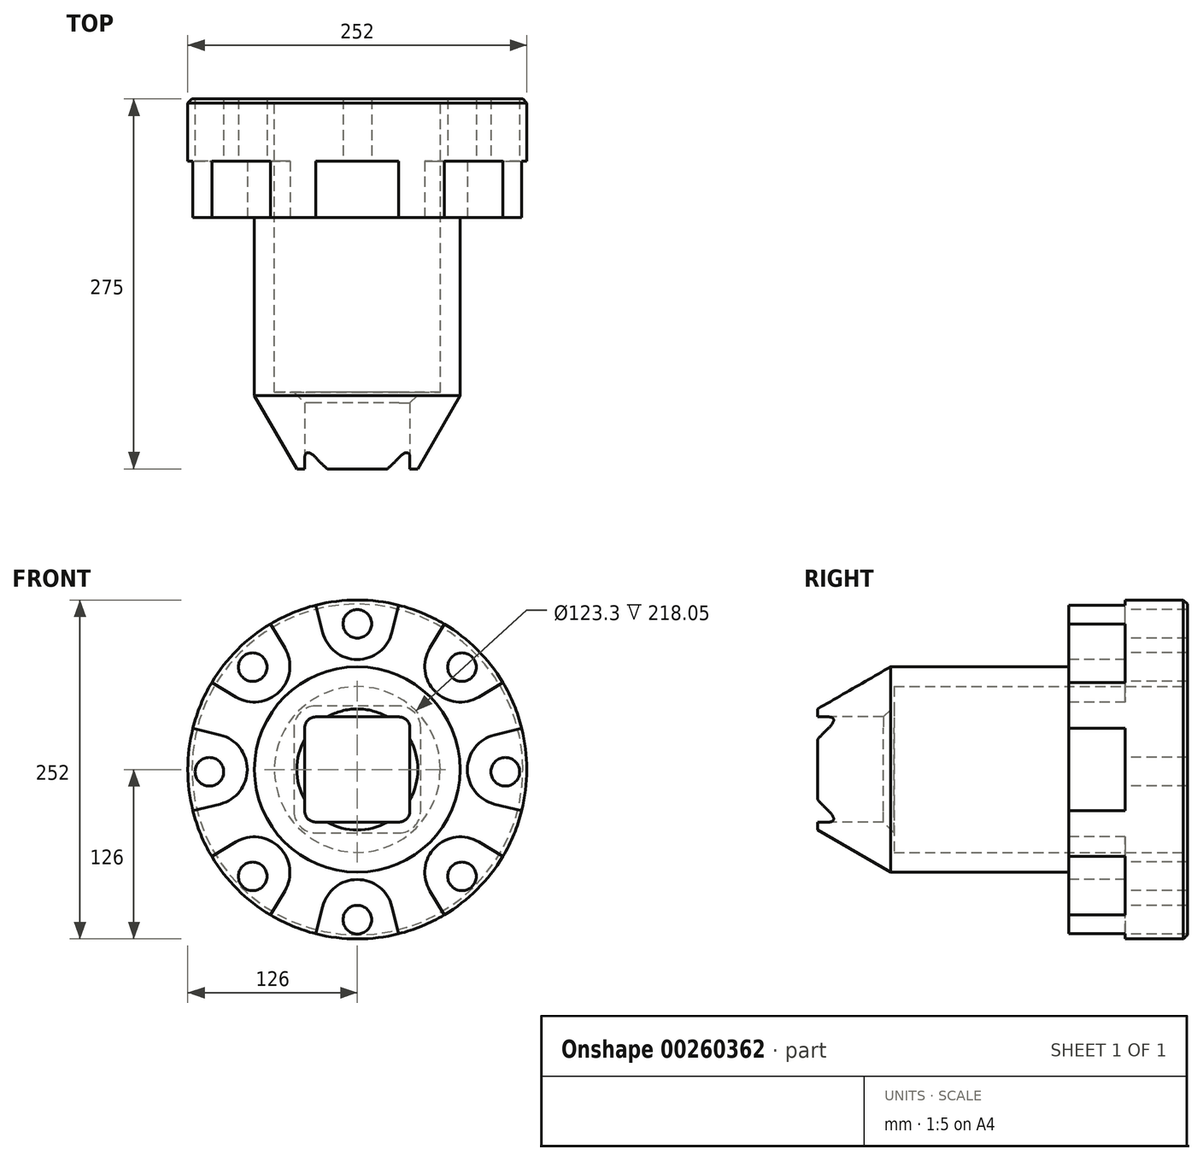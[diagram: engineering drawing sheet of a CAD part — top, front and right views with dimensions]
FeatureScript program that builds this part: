
annotation { "Feature Type Name" : "Feature", "Feature Type Description" : "" }
export const myFeature = defineFeature(function(context is Context, id is Id, definition is map)
    precondition{}
    {
        {
            var Q0;
            Q0=qCreatedBy(makeId("Front.planeOp"),FACE);
            var sketch = newSketch(context, id + "F0", { "sketchPlane" : qUnion([Q0])});
            skCircle(sketch, "E0", {"center": v(0, 0) * mm, "radius": 126 * mm});
            skSolve(sketch);
        }
        {
            var Q0;
            Q0 = qSketchRegion(id + "F0", true);
            extrude(context, id + "F1", {"entities" : qUnion([Q0]), "depth" : 275 * mm});
        }
        {
            var Q0;
            Q0=makeQuery(id+"F1.opExtrude","CAP_FACE",FACE,{"disambiguationData":[OSD([sQuery(id+"F0.wireOp",EDGE,"E0")])],"isStart":false});
            var sketch = newSketch(context, id + "F2", { "sketchPlane" : qUnion([Q0])});
            skCircle(sketch, "E1", {"center": v(0, 0) * mm, "radius": 76.45 * mm});
            skSolve(sketch);
        }
        {
            var Q0;
            Q0=makeQuery(id+"F2.imprint","IMPRINT",FACE,{"disambiguationData":[TD([[makeQuery(id+"F2.imprint","IMPRINT",EDGE,{"derivedFrom":sQuery(id+"F2.wireOp",EDGE,"E1")}),-1.0]])]});
            extrude(context, id + "F3", {"entities" : qUnion([Q0]), "operationType" : NewBodyOperationType.REMOVE, "oppositeDirection" : true, "depth" : (275 - 88.25) * mm});
        }
        {
            var Q0;
            Q0=makeQuery(id+"F3.boolean.opBoolean","COPY",FACE,{"derivedFrom":makeQuery(id+"F3.opExtrude","CAP_FACE",FACE,{"disambiguationData":[OSD([sQuery(id+"F0.wireOp",EDGE,"E0"),sQuery(id+"F2.wireOp",EDGE,"E1")])],"isStart":false})});
            var sketch = newSketch(context, id + "F4", { "sketchPlane" : qUnion([Q0])});
            skCircle(sketch, "E2", {"center": v(0, 108.32) * mm, "radius": 10.62 * mm});
            skCircle(sketch, "E3.1.0", {"center": v(-77.78, 76.1) * mm, "radius": 10.62 * mm});
            skCircle(sketch, "E3.2.0", {"center": v(-110, -1.68) * mm, "radius": 10.62 * mm});
            skCircle(sketch, "E3.3.0", {"center": v(-77.78, -79.46) * mm, "radius": 10.62 * mm});
            skCircle(sketch, "E3.4.0", {"center": v(0, -111.68) * mm, "radius": 10.62 * mm});
            skCircle(sketch, "E3.5.0", {"center": v(77.78, -79.46) * mm, "radius": 10.62 * mm});
            skCircle(sketch, "E3.6.0", {"center": v(110, -1.68) * mm, "radius": 10.62 * mm});
            skCircle(sketch, "E3.7.0", {"center": v(77.78, 76.1) * mm, "radius": 10.62 * mm});
            skPoint(sketch, "E3.center", {"position": v(0, -1.68) * mm});
            skSolve(sketch);
        }
        {
            var Q0;
            Q0 = qSketchRegion(id + "F4", true);
            extrude(context, id + "F5", {"entities" : qUnion([Q0]), "operationType" : NewBodyOperationType.REMOVE, "oppositeDirection" : true, "depth" : 25 * mm});
        }
        {
            var Q0;
            Q0 = qSketchRegion(id + "F4", true);
            extrude(context, id + "F6", {"entities" : qUnion([Q0]), "operationType" : NewBodyOperationType.REMOVE, "oppositeDirection" : true, "depth" : 169 * mm});
        }
        {
            var Q0;
            Q0=makeQuery(id+"F3.boolean.opBoolean","COPY",FACE,{"derivedFrom":makeQuery(id+"F3.opExtrude","CAP_FACE",FACE,{"disambiguationData":[OSD([sQuery(id+"F0.wireOp",EDGE,"E0"),sQuery(id+"F2.wireOp",EDGE,"E1")])],"isStart":false})});
            var sketch = newSketch(context, id + "F7", { "sketchPlane" : qUnion([Q0])});
            skPoint(sketch, "E4.center", {"position": v(0, 0) * mm});
            skArc(sketch, "E5", {"start": v(-25.71, 101.9) * mm, "mid": v(0, 81.82) * mm, "end": v(25.71, 101.9) * mm});
            skLineSegment(sketch, "E6", {"start": v(25.71, 101.9) * mm, "end": v(36.8, 146.37) * mm});
            skLineSegment(sketch, "E7", {"start": v(36.8, 146.37) * mm, "end": v(-36.8, 146.37) * mm});
            skLineSegment(sketch, "E8.MirrorCS", {"start": v(-25.71, 101.9) * mm, "end": v(-36.8, 146.37) * mm});
            skLineSegment(sketch, "E9.1.0", {"start": v(-77.48, 129.52) * mm, "end": v(-129.52, 77.48) * mm});
            skLineSegment(sketch, "E9.1.1", {"start": v(-53.88, 90.24) * mm, "end": v(-77.48, 129.52) * mm});
            skArc(sketch, "E9.1.2", {"start": v(-90.24, 53.88) * mm, "mid": v(-57.85, 57.85) * mm, "end": v(-53.88, 90.24) * mm});
            skLineSegment(sketch, "E9.1.3", {"start": v(-90.24, 53.88) * mm, "end": v(-129.52, 77.48) * mm});
            skLineSegment(sketch, "E9.2.0", {"start": v(-146.37, 36.8) * mm, "end": v(-146.37, -36.8) * mm});
            skLineSegment(sketch, "E9.2.1", {"start": v(-101.9, 25.71) * mm, "end": v(-146.37, 36.8) * mm});
            skArc(sketch, "E9.2.2", {"start": v(-101.9, -25.71) * mm, "mid": v(-81.82, 0) * mm, "end": v(-101.9, 25.71) * mm});
            skLineSegment(sketch, "E9.2.3", {"start": v(-101.9, -25.71) * mm, "end": v(-146.37, -36.8) * mm});
            skLineSegment(sketch, "E9.3.0", {"start": v(-129.52, -77.48) * mm, "end": v(-77.48, -129.52) * mm});
            skLineSegment(sketch, "E9.3.1", {"start": v(-90.24, -53.88) * mm, "end": v(-129.52, -77.48) * mm});
            skArc(sketch, "E9.3.2", {"start": v(-53.88, -90.24) * mm, "mid": v(-57.85, -57.85) * mm, "end": v(-90.24, -53.88) * mm});
            skLineSegment(sketch, "E9.3.3", {"start": v(-53.88, -90.24) * mm, "end": v(-77.48, -129.52) * mm});
            skLineSegment(sketch, "E9.4.0", {"start": v(-36.8, -146.37) * mm, "end": v(36.8, -146.37) * mm});
            skLineSegment(sketch, "E9.4.1", {"start": v(-25.71, -101.9) * mm, "end": v(-36.8, -146.37) * mm});
            skArc(sketch, "E9.4.2", {"start": v(25.71, -101.9) * mm, "mid": v(0, -81.82) * mm, "end": v(-25.71, -101.9) * mm});
            skLineSegment(sketch, "E9.4.3", {"start": v(25.71, -101.9) * mm, "end": v(36.8, -146.37) * mm});
            skLineSegment(sketch, "E9.5.0", {"start": v(77.48, -129.52) * mm, "end": v(129.52, -77.48) * mm});
            skLineSegment(sketch, "E9.5.1", {"start": v(53.88, -90.24) * mm, "end": v(77.48, -129.52) * mm});
            skArc(sketch, "E9.5.2", {"start": v(90.24, -53.88) * mm, "mid": v(57.85, -57.85) * mm, "end": v(53.88, -90.24) * mm});
            skLineSegment(sketch, "E9.5.3", {"start": v(90.24, -53.88) * mm, "end": v(129.52, -77.48) * mm});
            skLineSegment(sketch, "E9.6.0", {"start": v(146.37, -36.8) * mm, "end": v(146.37, 36.8) * mm});
            skLineSegment(sketch, "E9.6.1", {"start": v(101.9, -25.71) * mm, "end": v(146.37, -36.8) * mm});
            skArc(sketch, "E9.6.2", {"start": v(101.9, 25.71) * mm, "mid": v(81.82, 0) * mm, "end": v(101.9, -25.71) * mm});
            skLineSegment(sketch, "E9.6.3", {"start": v(101.9, 25.71) * mm, "end": v(146.37, 36.8) * mm});
            skLineSegment(sketch, "E9.7.0", {"start": v(129.52, 77.48) * mm, "end": v(77.48, 129.52) * mm});
            skLineSegment(sketch, "E9.7.1", {"start": v(90.24, 53.88) * mm, "end": v(129.52, 77.48) * mm});
            skArc(sketch, "E9.7.2", {"start": v(53.88, 90.24) * mm, "mid": v(57.85, 57.85) * mm, "end": v(90.24, 53.88) * mm});
            skLineSegment(sketch, "E9.7.3", {"start": v(53.88, 90.24) * mm, "end": v(77.48, 129.52) * mm});
            skSolve(sketch);
        }
        {
            var Q0;
            Q0 = qSketchRegion(id + "F7", true);
            extrude(context, id + "F8", {"entities" : qUnion([Q0]), "operationType" : NewBodyOperationType.REMOVE, "oppositeDirection" : true, "depth" : 42 * mm});
        }
        {
            var Q0;
            Q0=makeQuery(id+"F1.opExtrude","CAP_EDGE",EDGE,{"disambiguationData":[OSD([sQuery(id+"F0.wireOp",EDGE,"E0")])],"isStart":true});
            chamfer(context, id + "F9", {"entities" : qUnion([Q0]), "width" : 3 * mm, "tangentPropagation" : true});
        }
        {
            var Q0;
            Q0=makeQuery(id+"F1.opExtrude","CAP_FACE",FACE,{"disambiguationData":[OSD([sQuery(id+"F0.wireOp",EDGE,"E0")])],"isStart":true});
            var sketch = newSketch(context, id + "F10", { "sketchPlane" : qUnion([Q0])});
            skCircle(sketch, "E10", {"center": v(0, 0) * mm, "radius": 61.65 * mm});
            skSolve(sketch);
        }
        {
            var Q0;
            Q0 = qSketchRegion(id + "F10", true);
            extrude(context, id + "F11", {"entities" : qUnion([Q0]), "operationType" : NewBodyOperationType.REMOVE, "oppositeDirection" : true, "depth" : 218.05 * mm});
        }
        {
            var Q0;
            Q0=qCreatedBy(makeId("Right.planeOp"),FACE);
            var sketch = newSketch(context, id + "F12", { "sketchPlane" : qUnion([Q0])});
            skLineSegment(sketch, "E11", {"start": v(0, 0) * mm, "end": v(-413.22, 0) * mm});
            skPoint(sketch, "E12.orphan", {"position": v(-249.17, 45) * mm});
            skLineSegment(sketch, "E13", {"start": v(-275, 45) * mm, "end": v(-210.73, 82.1) * mm});
            skLineSegment(sketch, "E14", {"start": v(-210.73, 82.1) * mm, "end": v(-287.5, 86.1) * mm});
            skLineSegment(sketch, "E15", {"start": v(-287.5, 86.1) * mm, "end": v(-275, 45) * mm});
            skSolve(sketch);
        }
        {
            var Q0;
            Q0 = qSketchRegion(id + "F12", true);
            var Q1;
            Q1=sQuery(id+"F12.wireOp",EDGE,"E11");
            revolve(context, id + "F13", {"operationType" : NewBodyOperationType.REMOVE, "entities" : qUnion([Q0]), "axis" : qUnion([Q1]), "revolveType" : RevolveType.FULL, "oppositeDirection" : true});
        }
        {
            var Q0;
            Q0=makeQuery(id+"F1.opExtrude","CAP_FACE",FACE,{"disambiguationData":[OSD([sQuery(id+"F0.wireOp",EDGE,"E0")])],"isStart":false});
            var sketch = newSketch(context, id + "F14", { "sketchPlane" : qUnion([Q0])});
            skLineSegment(sketch, "E16.bottom", {"start": v(-39.07, -39.08) * mm, "end": v(39.08, -39.08) * mm});
            skLineSegment(sketch, "E16.top", {"start": v(-39.08, 39.08) * mm, "end": v(39.08, 39.08) * mm});
            skLineSegment(sketch, "E16.left", {"start": v(-39.08, -39.08) * mm, "end": v(-39.08, 39.08) * mm});
            skLineSegment(sketch, "E16.right", {"start": v(39.08, -39.08) * mm, "end": v(39.08, 39.08) * mm});
            skPoint(sketch, "E16.middle", {"position": v(0, 0) * mm});
            skSolve(sketch);
        }
        {
            var Q0;
            Q0 = qSketchRegion(id + "F14", true);
            extrude(context, id + "F15", {"entities" : qUnion([Q0]), "operationType" : NewBodyOperationType.REMOVE, "oppositeDirection" : true, "depth" : 60 * mm});
        }
        {
            var Q0;
            Q0=makeQuery(id+"F15.boolean.opBoolean","COPY",EDGE,{"derivedFrom":makeQuery(id+"F15.opExtrude","SWEPT_EDGE",EDGE,{"disambiguationData":[OSD([sQuery(id+"F14.wireOp",EDGE,"E16.bottom"),sQuery(id+"F14.wireOp",EDGE,"E16.left")])]})});
            fillet(context, id + "F16", {"entities" : qUnion([Q0]), "radius" : 8 * mm, "tangentPropagation" : true, "allowEdgeOverflow" : false});
        }
        {
            var Q0;
            Q0=makeQuery(id+"F15.boolean.opBoolean","COPY",EDGE,{"derivedFrom":makeQuery(id+"F15.opExtrude","SWEPT_EDGE",EDGE,{"disambiguationData":[OSD([sQuery(id+"F14.wireOp",EDGE,"E16.top"),sQuery(id+"F14.wireOp",EDGE,"E16.right")])]})});
            fillet(context, id + "F17", {"entities" : qUnion([Q0]), "radius" : 8 * mm, "tangentPropagation" : true, "allowEdgeOverflow" : false});
        }
        {
            var Q0;
            Q0=makeQuery(id+"F15.boolean.opBoolean","COPY",EDGE,{"derivedFrom":makeQuery(id+"F15.opExtrude","SWEPT_EDGE",EDGE,{"disambiguationData":[OSD([sQuery(id+"F14.wireOp",EDGE,"E16.top"),sQuery(id+"F14.wireOp",EDGE,"E16.left")])]})});
            fillet(context, id + "F18", {"entities" : qUnion([Q0]), "radius" : 8 * mm, "tangentPropagation" : true, "allowEdgeOverflow" : false});
        }
        {
            var Q0;
            Q0=makeQuery(id+"F15.boolean.opBoolean","COPY",EDGE,{"derivedFrom":makeQuery(id+"F15.opExtrude","SWEPT_EDGE",EDGE,{"disambiguationData":[OSD([sQuery(id+"F14.wireOp",EDGE,"E16.bottom"),sQuery(id+"F14.wireOp",EDGE,"E16.right")])]})});
            fillet(context, id + "F19", {"entities" : qUnion([Q0]), "radius" : 8 * mm, "tangentPropagation" : true, "allowEdgeOverflow" : false});
        }
        {
            var Q0;
            Q0=makeQuery(id+"F15.boolean.opBoolean","INTERSECT",EDGE,{"derivedFrom":[makeQuery(id+"F11.boolean.opBoolean","COPY",FACE,{"derivedFrom":makeQuery(id+"F11.opExtrude","CAP_FACE",FACE,{"disambiguationData":[OSD([sQuery(id+"F10.wireOp",EDGE,"E10")])],"isStart":false})}),makeQuery(id+"F15.opExtrude","SWEPT_FACE",FACE,{"disambiguationData":[OSD([sQuery(id+"F14.wireOp",EDGE,"E16.left")])]})]});
            var Q1;
            Q1=makeQuery(id+"F18.opFillet","BLEND_EDGE",EDGE,{"blendedFrom":[makeQuery(id+"F15.boolean.opBoolean","COPY",EDGE,{"derivedFrom":makeQuery(id+"F15.opExtrude","SWEPT_EDGE",EDGE,{"disambiguationData":[OSD([sQuery(id+"F14.wireOp",EDGE,"E16.top"),sQuery(id+"F14.wireOp",EDGE,"E16.left")])]})}),makeQuery(id+"F11.boolean.opBoolean","COPY",FACE,{"derivedFrom":makeQuery(id+"F11.opExtrude","CAP_FACE",FACE,{"disambiguationData":[OSD([sQuery(id+"F10.wireOp",EDGE,"E10")])],"isStart":false})})],"blendedInto":[makeQuery(id+"F11.boolean.opBoolean","COPY",FACE,{"derivedFrom":makeQuery(id+"F11.opExtrude","CAP_FACE",FACE,{"disambiguationData":[OSD([sQuery(id+"F10.wireOp",EDGE,"E10")])],"isStart":false})})]});
            var Q2;
            Q2=makeQuery(id+"F15.boolean.opBoolean","INTERSECT",EDGE,{"derivedFrom":[makeQuery(id+"F11.boolean.opBoolean","COPY",FACE,{"derivedFrom":makeQuery(id+"F11.opExtrude","CAP_FACE",FACE,{"disambiguationData":[OSD([sQuery(id+"F10.wireOp",EDGE,"E10")])],"isStart":false})}),makeQuery(id+"F15.opExtrude","SWEPT_FACE",FACE,{"disambiguationData":[OSD([sQuery(id+"F14.wireOp",EDGE,"E16.top")])]})]});
            var Q3;
            Q3=makeQuery(id+"F17.opFillet","BLEND_EDGE",EDGE,{"blendedFrom":[makeQuery(id+"F15.boolean.opBoolean","COPY",EDGE,{"derivedFrom":makeQuery(id+"F15.opExtrude","SWEPT_EDGE",EDGE,{"disambiguationData":[OSD([sQuery(id+"F14.wireOp",EDGE,"E16.top"),sQuery(id+"F14.wireOp",EDGE,"E16.right")])]})}),makeQuery(id+"F11.boolean.opBoolean","COPY",FACE,{"derivedFrom":makeQuery(id+"F11.opExtrude","CAP_FACE",FACE,{"disambiguationData":[OSD([sQuery(id+"F10.wireOp",EDGE,"E10")])],"isStart":false})})],"blendedInto":[makeQuery(id+"F11.boolean.opBoolean","COPY",FACE,{"derivedFrom":makeQuery(id+"F11.opExtrude","CAP_FACE",FACE,{"disambiguationData":[OSD([sQuery(id+"F10.wireOp",EDGE,"E10")])],"isStart":false})})]});
            var Q4;
            Q4=makeQuery(id+"F15.boolean.opBoolean","INTERSECT",EDGE,{"derivedFrom":[makeQuery(id+"F11.boolean.opBoolean","COPY",FACE,{"derivedFrom":makeQuery(id+"F11.opExtrude","CAP_FACE",FACE,{"disambiguationData":[OSD([sQuery(id+"F10.wireOp",EDGE,"E10")])],"isStart":false})}),makeQuery(id+"F15.opExtrude","SWEPT_FACE",FACE,{"disambiguationData":[OSD([sQuery(id+"F14.wireOp",EDGE,"E16.right")])]})]});
            var Q5;
            Q5=makeQuery(id+"F15.boolean.opBoolean","INTERSECT",EDGE,{"derivedFrom":[makeQuery(id+"F11.boolean.opBoolean","COPY",FACE,{"derivedFrom":makeQuery(id+"F11.opExtrude","CAP_FACE",FACE,{"disambiguationData":[OSD([sQuery(id+"F10.wireOp",EDGE,"E10")])],"isStart":false})}),makeQuery(id+"F15.opExtrude","SWEPT_FACE",FACE,{"disambiguationData":[OSD([sQuery(id+"F14.wireOp",EDGE,"E16.bottom")])]})]});
            var Q6;
            Q6=makeQuery(id+"F16.opFillet","BLEND_EDGE",EDGE,{"blendedFrom":[makeQuery(id+"F15.boolean.opBoolean","COPY",EDGE,{"derivedFrom":makeQuery(id+"F15.opExtrude","SWEPT_EDGE",EDGE,{"disambiguationData":[OSD([sQuery(id+"F14.wireOp",EDGE,"E16.bottom"),sQuery(id+"F14.wireOp",EDGE,"E16.left")])]})}),makeQuery(id+"F11.boolean.opBoolean","COPY",FACE,{"derivedFrom":makeQuery(id+"F11.opExtrude","CAP_FACE",FACE,{"disambiguationData":[OSD([sQuery(id+"F10.wireOp",EDGE,"E10")])],"isStart":false})})],"blendedInto":[makeQuery(id+"F11.boolean.opBoolean","COPY",FACE,{"derivedFrom":makeQuery(id+"F11.opExtrude","CAP_FACE",FACE,{"disambiguationData":[OSD([sQuery(id+"F10.wireOp",EDGE,"E10")])],"isStart":false})})]});
            var Q7;
            Q7=makeQuery(id+"F19.opFillet","BLEND_EDGE",EDGE,{"blendedFrom":[makeQuery(id+"F15.boolean.opBoolean","COPY",EDGE,{"derivedFrom":makeQuery(id+"F15.opExtrude","SWEPT_EDGE",EDGE,{"disambiguationData":[OSD([sQuery(id+"F14.wireOp",EDGE,"E16.bottom"),sQuery(id+"F14.wireOp",EDGE,"E16.right")])]})}),makeQuery(id+"F11.boolean.opBoolean","COPY",FACE,{"derivedFrom":makeQuery(id+"F11.opExtrude","CAP_FACE",FACE,{"disambiguationData":[OSD([sQuery(id+"F10.wireOp",EDGE,"E10")])],"isStart":false})})],"blendedInto":[makeQuery(id+"F11.boolean.opBoolean","COPY",FACE,{"derivedFrom":makeQuery(id+"F11.opExtrude","CAP_FACE",FACE,{"disambiguationData":[OSD([sQuery(id+"F10.wireOp",EDGE,"E10")])],"isStart":false})})]});
            chamfer(context, id + "F20", {"entities" : qUnion([Q0, Q1, Q2, Q3, Q4, Q5, Q6, Q7]), "width" : 8 * mm, "tangentPropagation" : true});
        }
    });
